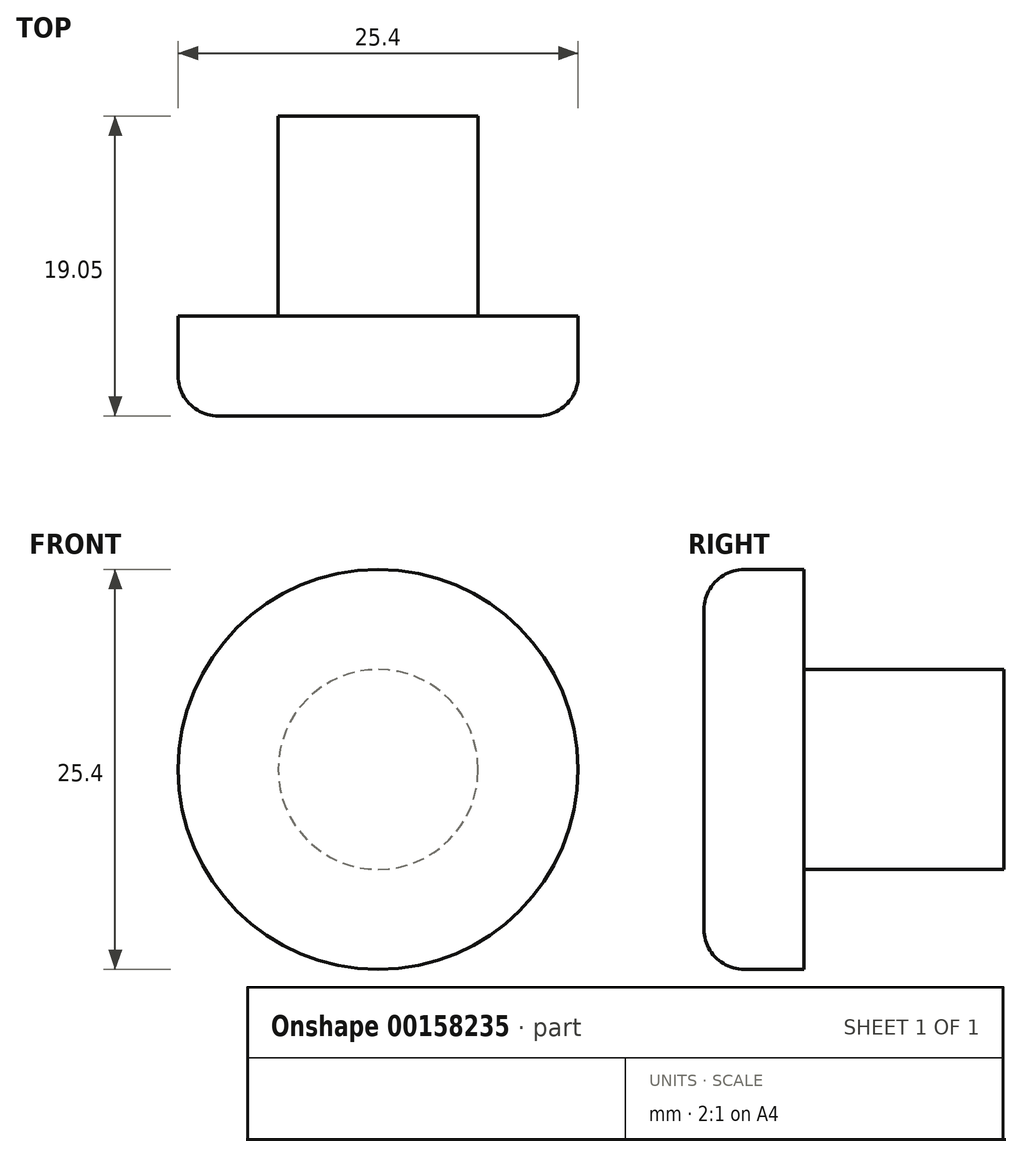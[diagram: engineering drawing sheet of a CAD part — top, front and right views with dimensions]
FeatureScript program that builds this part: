
annotation { "Feature Type Name" : "Feature", "Feature Type Description" : "" }
export const myFeature = defineFeature(function(context is Context, id is Id, definition is map)
    precondition{}
    {
        {
            var Q0;
            Q0=qCreatedBy(makeId("Front.planeOp"),FACE);
            var sketch = newSketch(context, id + "F0", { "sketchPlane" : qUnion([Q0])});
            skCircle(sketch, "E0", {"center": v(0, 0) * mm, "radius": 6.35 * mm});
            skSolve(sketch);
        }
        {
            var Q0;
            Q0 = qSketchRegion(id + "F0", true);
            extrude(context, id + "F1", {"entities" : qUnion([Q0]), "endBound" : BoundingType.SYMMETRIC, "depth" : 12.7 * mm});
        }
        {
            var Q0;
            Q0=makeQuery(id+"F1.opExtrude","CAP_FACE",FACE,{"disambiguationData":[OSD([sQuery(id+"F0.wireOp",EDGE,"E0")])],"isStart":false});
            var sketch = newSketch(context, id + "F2", { "sketchPlane" : qUnion([Q0])});
            skCircle(sketch, "E1", {"center": v(0, 0) * mm, "radius": 12.7 * mm});
            skSolve(sketch);
        }
        {
            var Q0;
            Q0 = qSketchRegion(id + "F2", true);
            extrude(context, id + "F3", {"entities" : qUnion([Q0]), "operationType" : NewBodyOperationType.ADD, "depth" : 6.35 * mm});
        }
        {
            var Q0;
            Q0=makeQuery(id+"F3.opExtrude","CAP_EDGE",EDGE,{"disambiguationData":[OSD([sQuery(id+"F2.wireOp",EDGE,"E1")])],"isStart":false});
            fillet(context, id + "F4", {"entities" : qUnion([Q0]), "radius" : 2.54 * mm, "tangentPropagation" : true, "allowEdgeOverflow" : false});
        }
    });
